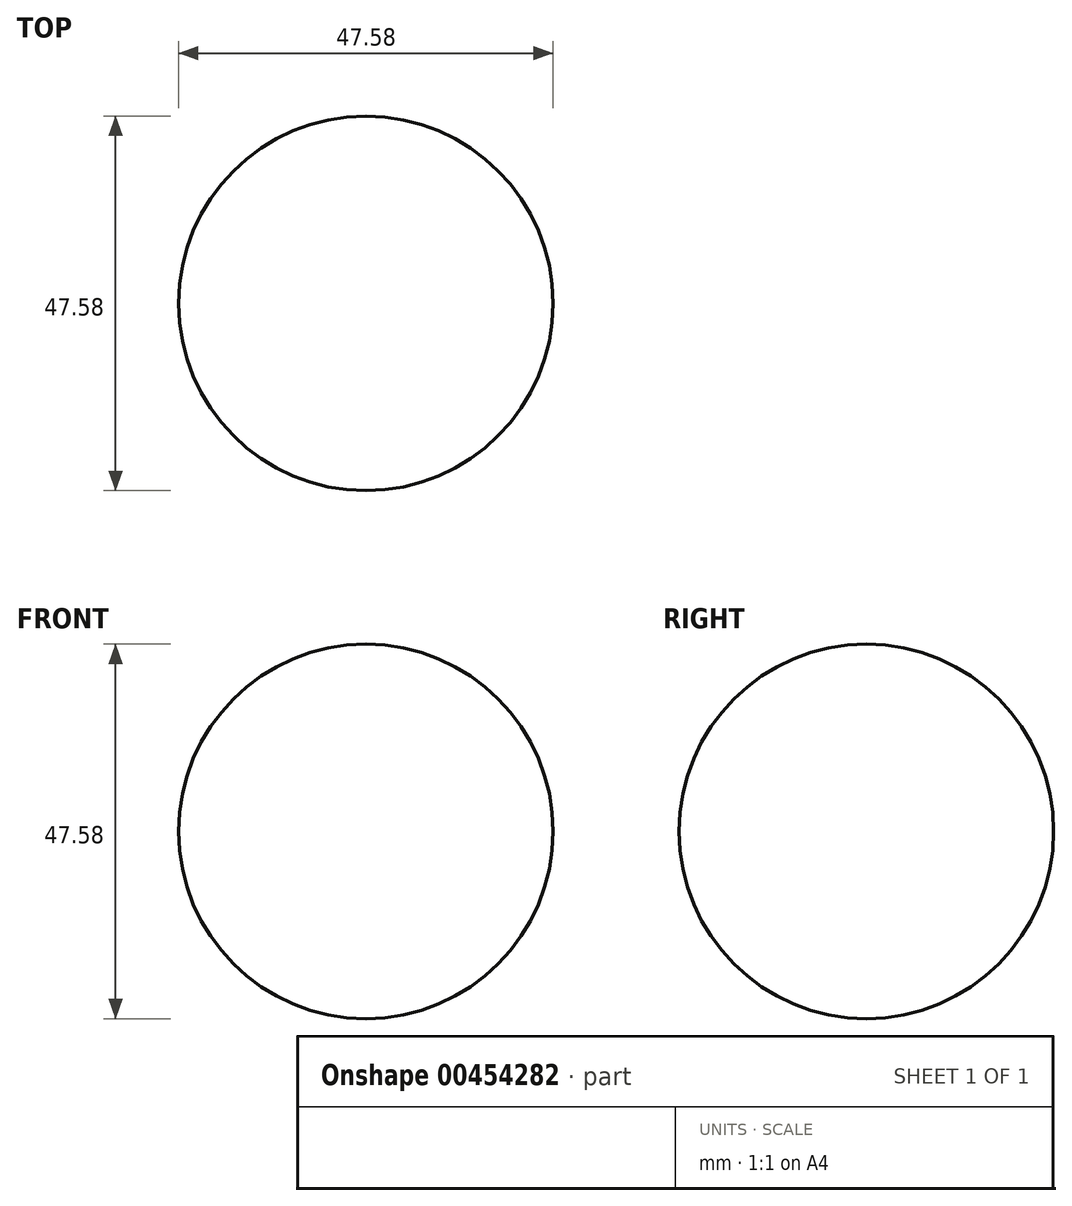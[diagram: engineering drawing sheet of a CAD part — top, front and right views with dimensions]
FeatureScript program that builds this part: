
annotation { "Feature Type Name" : "Feature", "Feature Type Description" : "" }
export const myFeature = defineFeature(function(context is Context, id is Id, definition is map)
    precondition{}
    {
        {
            var Q0;
            Q0=qCreatedBy(makeId("Front.planeOp"),FACE);
            var sketch = newSketch(context, id + "F0", { "sketchPlane" : qUnion([Q0])});
            skCircle(sketch, "E0", {"center": v(0, 0) * mm, "radius": 23.79 * mm});
            skLineSegment(sketch, "E1", {"start": v(0, 0) * mm, "end": v(-23.79, 0) * mm});
            skLineSegment(sketch, "E2", {"start": v(-23.79, 0) * mm, "end": v(23.79, 0) * mm});
            skSolve(sketch);
        }
        {
            var Q0;
            {var subQ0=sQuery(id+"F0.wireOp",EDGE,"E2");var subQ4=makeQuery(id+"F0.imprint","IMPRINT",VERTEX,{"derivedFrom":subQ0});Q0=makeQuery(id+"F0.imprint","IMPRINT",FACE,{"disambiguationData":[TD([[makeQuery(id+"F0.imprint","IMPRINT",EDGE,{"disambiguationData":[TD([[subQ4,1.0]])],"derivedFrom":subQ0}),-1.0]])]});}
            var Q1;
            Q1=sQuery(id+"F0.wireOp",EDGE,"E2");
            revolve(context, id + "F1", {"surfaceOperationType" : NewSurfaceOperationType.NEW, "entities" : qUnion([Q0]), "axis" : qUnion([Q1]), "revolveType" : RevolveType.FULL});
        }
    });
